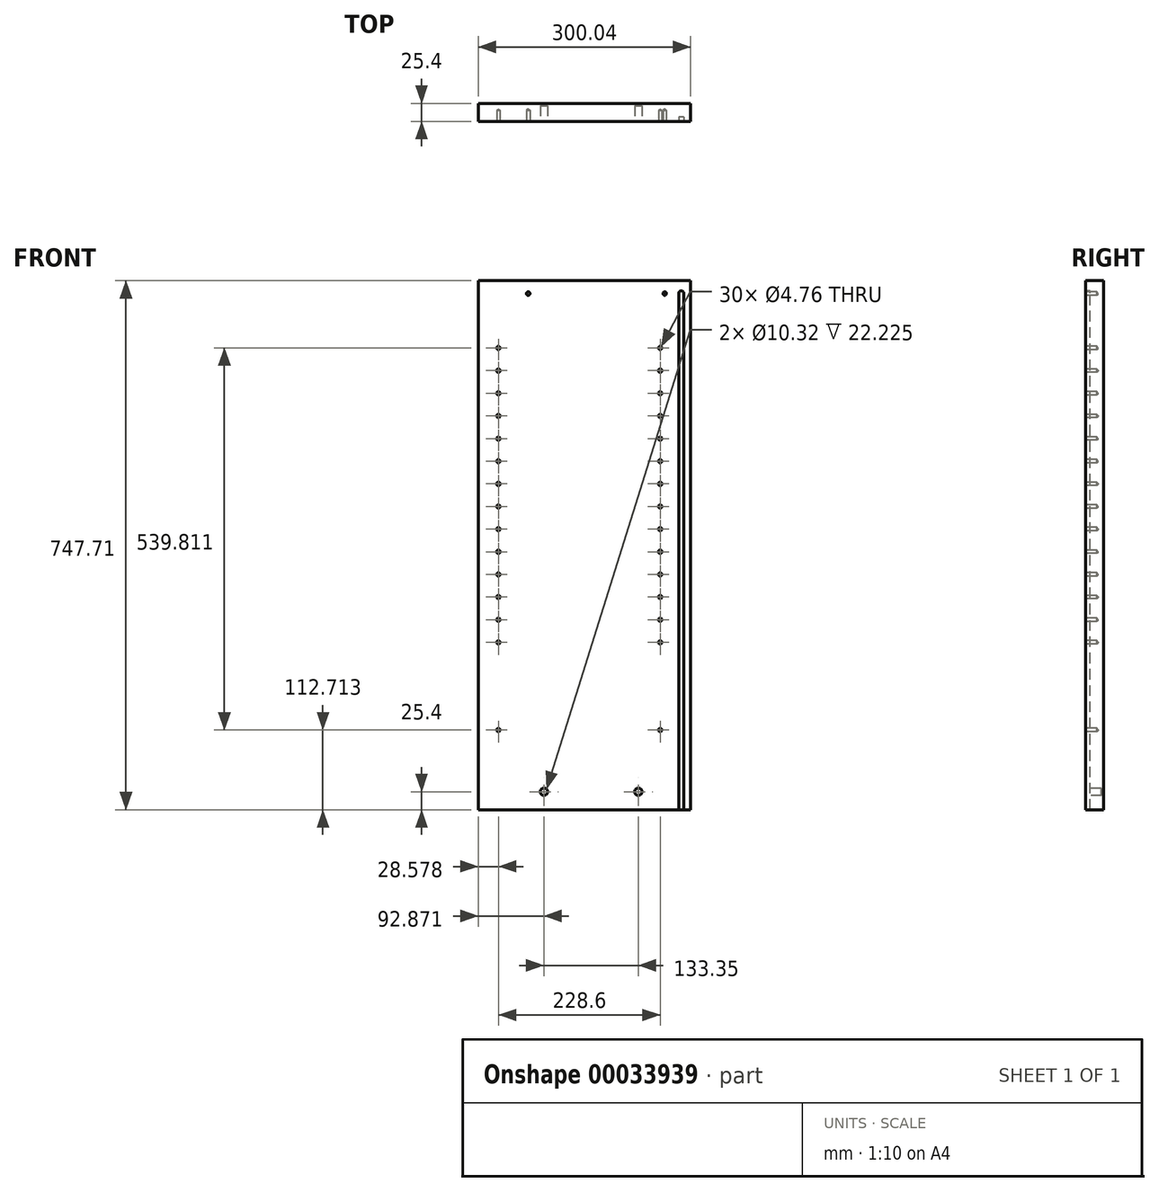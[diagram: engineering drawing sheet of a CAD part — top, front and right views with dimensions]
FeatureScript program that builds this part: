
annotation { "Feature Type Name" : "Feature", "Feature Type Description" : "" }
export const myFeature = defineFeature(function(context is Context, id is Id, definition is map)
    precondition{}
    {
        {
            var Q0;
            Q0=qCreatedBy(makeId("Front.planeOp"),FACE);
            var sketch = newSketch(context, id + "F0", { "sketchPlane" : qUnion([Q0])});
            skLineSegment(sketch, "E0.bottom", {"start": v(0, 0) * mm, "end": v(-300.04, 0) * mm});
            skLineSegment(sketch, "E0.top", {"start": v(0, 747.71) * mm, "end": v(-300.04, 747.71) * mm});
            skLineSegment(sketch, "E0.left", {"start": v(0, 0) * mm, "end": v(0, 747.71) * mm});
            skLineSegment(sketch, "E0.right", {"start": v(-300.04, 0) * mm, "end": v(-300.04, 747.71) * mm});
            skSolve(sketch);
        }
        {
            var Q0;
            Q0=makeQuery(id+"F0.imprint","IMPRINT",FACE,{"disambiguationData":[TD([[makeQuery(id+"F0.imprint","IMPRINT",EDGE,{"derivedFrom":sQuery(id+"F0.wireOp",EDGE,"E0.bottom")}),-1.0]])]});
            extrude(context, id + "F1", {"entities" : qUnion([Q0]), "depth" : 25.4 * mm});
        }
        {
            var Q0;
            Q0=makeQuery(id+"F1.opExtrude","CAP_FACE",FACE,{"disambiguationData":[OSD([sQuery(id+"F0.wireOp",EDGE,"E0.bottom"),sQuery(id+"F0.wireOp",EDGE,"E0.top"),sQuery(id+"F0.wireOp",EDGE,"E0.left"),sQuery(id+"F0.wireOp",EDGE,"E0.right")])],"isStart":false});
            var sketch = newSketch(context, id + "F2", { "sketchPlane" : qUnion([Q0])});
            skPoint(sketch, "E1", {"position": v(-271.46, 112.71) * mm});
            skPoint(sketch, "E2", {"position": v(-42.86, 112.71) * mm});
            skPoint(sketch, "E3", {"position": v(-42.86, 236.54) * mm});
            skPoint(sketch, "E4", {"position": v(-271.46, 236.54) * mm});
            skPoint(sketch, "E5.0.1.0", {"position": v(-271.46, 268.54) * mm});
            skPoint(sketch, "E5.0.1.1", {"position": v(-42.86, 268.54) * mm});
            skPoint(sketch, "E5.0.2.0", {"position": v(-271.46, 300.54) * mm});
            skPoint(sketch, "E5.0.2.1", {"position": v(-42.86, 300.54) * mm});
            skPoint(sketch, "E5.0.3.0", {"position": v(-271.46, 332.53) * mm});
            skPoint(sketch, "E5.0.3.1", {"position": v(-42.86, 332.53) * mm});
            skPoint(sketch, "E5.0.4.0", {"position": v(-271.46, 364.53) * mm});
            skPoint(sketch, "E5.0.4.1", {"position": v(-42.86, 364.53) * mm});
            skPoint(sketch, "E5.0.5.0", {"position": v(-271.46, 396.53) * mm});
            skPoint(sketch, "E5.0.5.1", {"position": v(-42.86, 396.53) * mm});
            skPoint(sketch, "E5.0.6.0", {"position": v(-271.46, 428.53) * mm});
            skPoint(sketch, "E5.0.6.1", {"position": v(-42.86, 428.53) * mm});
            skPoint(sketch, "E5.0.7.0", {"position": v(-271.46, 460.53) * mm});
            skPoint(sketch, "E5.0.7.1", {"position": v(-42.86, 460.53) * mm});
            skPoint(sketch, "E5.0.8.0", {"position": v(-271.46, 492.53) * mm});
            skPoint(sketch, "E5.0.8.1", {"position": v(-42.86, 492.53) * mm});
            skPoint(sketch, "E5.0.9.0", {"position": v(-271.46, 524.53) * mm});
            skPoint(sketch, "E5.0.9.1", {"position": v(-42.86, 524.53) * mm});
            skPoint(sketch, "E5.0.10.0", {"position": v(-271.46, 556.53) * mm});
            skPoint(sketch, "E5.0.10.1", {"position": v(-42.86, 556.53) * mm});
            skPoint(sketch, "E5.0.11.0", {"position": v(-271.46, 588.53) * mm});
            skPoint(sketch, "E5.0.11.1", {"position": v(-42.86, 588.53) * mm});
            skPoint(sketch, "E5.0.12.0", {"position": v(-271.46, 620.52) * mm});
            skPoint(sketch, "E5.0.12.1", {"position": v(-42.86, 620.52) * mm});
            skPoint(sketch, "E5.0.13.0", {"position": v(-271.46, 652.52) * mm});
            skPoint(sketch, "E5.0.13.1", {"position": v(-42.86, 652.52) * mm});
            skLineSegment(sketch, "E5.direction1", {"start": v(-271.46, 236.54) * mm, "end": v(-246.06, 236.54) * mm, "construction": true});
            skLineSegment(sketch, "E5.direction2", {"start": v(-271.46, 236.54) * mm, "end": v(-271.46, 268.54) * mm, "construction": true});
            skSolve(sketch);
        }
        {
            var Q0;
            Q0=sQuery(id+"F2.wireOp",VERTEX,"E1");
            var Q1;
            Q1=sQuery(id+"F2.wireOp",VERTEX,"E2");
            var Q2;
            Q2=sQuery(id+"F2.wireOp",VERTEX,"E4");
            var Q3;
            Q3=sQuery(id+"F2.wireOp",VERTEX,"E5.0.1.0");
            var Q4;
            Q4=sQuery(id+"F2.wireOp",VERTEX,"E3");
            var Q5;
            Q5=sQuery(id+"F2.wireOp",VERTEX,"E5.0.1.1");
            var Q6;
            Q6=sQuery(id+"F2.wireOp",VERTEX,"E5.0.2.1");
            var Q7;
            Q7=sQuery(id+"F2.wireOp",VERTEX,"E5.0.2.0");
            var Q8;
            Q8=sQuery(id+"F2.wireOp",VERTEX,"E5.0.3.0");
            var Q9;
            Q9=sQuery(id+"F2.wireOp",VERTEX,"E5.0.4.0");
            var Q10;
            Q10=sQuery(id+"F2.wireOp",VERTEX,"E5.0.5.0");
            var Q11;
            Q11=sQuery(id+"F2.wireOp",VERTEX,"E5.0.6.0");
            var Q12;
            Q12=sQuery(id+"F2.wireOp",VERTEX,"E5.0.7.0");
            var Q13;
            Q13=sQuery(id+"F2.wireOp",VERTEX,"E5.0.8.0");
            var Q14;
            Q14=sQuery(id+"F2.wireOp",VERTEX,"E5.0.9.0");
            var Q15;
            Q15=sQuery(id+"F2.wireOp",VERTEX,"E5.0.10.0");
            var Q16;
            Q16=sQuery(id+"F2.wireOp",VERTEX,"E5.0.12.0");
            var Q17;
            Q17=sQuery(id+"F2.wireOp",VERTEX,"E5.0.13.0");
            var Q18;
            Q18=sQuery(id+"F2.wireOp",VERTEX,"E5.0.3.1");
            var Q19;
            Q19=sQuery(id+"F2.wireOp",VERTEX,"E5.0.4.1");
            var Q20;
            Q20=sQuery(id+"F2.wireOp",VERTEX,"E5.0.5.1");
            var Q21;
            Q21=sQuery(id+"F2.wireOp",VERTEX,"E5.0.6.1");
            var Q22;
            Q22=sQuery(id+"F2.wireOp",VERTEX,"E5.0.4.1");
            var Q23;
            Q23=sQuery(id+"F2.wireOp",VERTEX,"E5.0.7.1");
            var Q24;
            Q24=sQuery(id+"F2.wireOp",VERTEX,"E5.0.8.1");
            var Q25;
            Q25=sQuery(id+"F2.wireOp",VERTEX,"E5.0.9.1");
            var Q26;
            Q26=sQuery(id+"F2.wireOp",VERTEX,"E5.0.10.1");
            var Q27;
            Q27=sQuery(id+"F2.wireOp",VERTEX,"E5.0.11.1");
            var Q28;
            Q28=sQuery(id+"F2.wireOp",VERTEX,"E5.0.12.1");
            var Q29;
            Q29=sQuery(id+"F2.wireOp",VERTEX,"E5.0.13.1");
            var Q30;
            Q30=sQuery(id+"F2.wireOp",VERTEX,"E5.0.11.0");
            var Q31;
            Q31=makeQuery(id+"F1.opExtrude","SWEPT_BODY",BODY,{"disambiguationData":[OSD([sQuery(id+"F0.wireOp",EDGE,"E0.bottom"),sQuery(id+"F0.wireOp",EDGE,"E0.top"),sQuery(id+"F0.wireOp",EDGE,"E0.left"),sQuery(id+"F0.wireOp",EDGE,"E0.right")])]});
            hole(context, id + "F3", {"style" : HoleStyle.SIMPLE, "holeDiameter" : 4.76 * mm, "endStyle" : HoleEndStyle.BLIND, "holeDepth" : 15.88 * mm, "locations" : qUnion([Q0, Q1, Q2, Q3, Q4, Q5, Q6, Q7, Q8, Q9, Q10, Q11, Q12, Q13, Q14, Q15, Q16, Q17, Q18, Q19, Q20, Q21, Q22, Q23, Q24, Q25, Q26, Q27, Q28, Q29, Q30]), "scope" : qUnion([Q31])});
        }
        {
            var Q0;
            Q0=makeQuery(id+"F1.opExtrude","CAP_FACE",FACE,{"disambiguationData":[OSD([sQuery(id+"F0.wireOp",EDGE,"E0.bottom"),sQuery(id+"F0.wireOp",EDGE,"E0.top"),sQuery(id+"F0.wireOp",EDGE,"E0.left"),sQuery(id+"F0.wireOp",EDGE,"E0.right")])],"isStart":false});
            var sketch = newSketch(context, id + "F4", { "sketchPlane" : qUnion([Q0])});
            skLineSegment(sketch, "E6.bottom", {"start": v(-9.53, 0) * mm, "end": v(-16.67, 0) * mm});
            skLineSegment(sketch, "E6.left", {"start": v(-9.53, 0) * mm, "end": v(-9.53, 729.85) * mm});
            skLineSegment(sketch, "E6.right", {"start": v(-16.67, 0) * mm, "end": v(-16.67, 729.85) * mm});
            skArc(sketch, "E7", {"start": v(-9.53, 729.85) * mm, "mid": v(-13.1, 733.42) * mm, "end": v(-16.67, 729.85) * mm});
            skSolve(sketch);
        }
        {
            var Q0;
            Q0 = qSketchRegion(id + "F4", true);
            extrude(context, id + "F5", {"entities" : qUnion([Q0]), "operationType" : NewBodyOperationType.REMOVE, "oppositeDirection" : true, "depth" : 6.35 * mm});
        }
        {
            var Q0;
            Q0=makeQuery(id+"F1.opExtrude","CAP_FACE",FACE,{"disambiguationData":[OSD([sQuery(id+"F0.wireOp",EDGE,"E0.bottom"),sQuery(id+"F0.wireOp",EDGE,"E0.top"),sQuery(id+"F0.wireOp",EDGE,"E0.left"),sQuery(id+"F0.wireOp",EDGE,"E0.right")])],"isStart":false});
            var sketch = newSketch(context, id + "F6", { "sketchPlane" : qUnion([Q0])});
            skCircle(sketch, "E8", {"center": v(-73.82, 25.4) * mm, "radius": 5.16 * mm});
            skCircle(sketch, "E9", {"center": v(-207.17, 25.4) * mm, "radius": 5.16 * mm});
            skSolve(sketch);
        }
        {
            var Q0;
            Q0 = qSketchRegion(id + "F6", true);
            extrude(context, id + "F7", {"entities" : qUnion([Q0]), "operationType" : NewBodyOperationType.REMOVE, "oppositeDirection" : true, "depth" : 22.22 * mm});
        }
        {
            var Q0;
            Q0=makeQuery(id+"F1.opExtrude","CAP_FACE",FACE,{"disambiguationData":[OSD([sQuery(id+"F0.wireOp",EDGE,"E0.bottom"),sQuery(id+"F0.wireOp",EDGE,"E0.top"),sQuery(id+"F0.wireOp",EDGE,"E0.left"),sQuery(id+"F0.wireOp",EDGE,"E0.right")])],"isStart":false});
            var sketch = newSketch(context, id + "F8", { "sketchPlane" : qUnion([Q0])});
            skPoint(sketch, "E10", {"position": v(-229.4, 729.46) * mm});
            skPoint(sketch, "E11", {"position": v(-36.51, 729.46) * mm});
            skSolve(sketch);
        }
        {
            var Q0;
            Q0=sQuery(id+"F8.wireOp",VERTEX,"E10");
            var Q1;
            Q1=sQuery(id+"F8.wireOp",VERTEX,"E11");
            var Q2;
            Q2=makeQuery(id+"F1.opExtrude","SWEPT_BODY",BODY,{"disambiguationData":[OSD([sQuery(id+"F0.wireOp",EDGE,"E0.bottom"),sQuery(id+"F0.wireOp",EDGE,"E0.top"),sQuery(id+"F0.wireOp",EDGE,"E0.left"),sQuery(id+"F0.wireOp",EDGE,"E0.right")])]});
            hole(context, id + "F9", {"style" : HoleStyle.SIMPLE, "holeDiameter" : 5 * mm, "endStyle" : HoleEndStyle.BLIND, "holeDepth" : 15.88 * mm, "locations" : qUnion([Q0, Q1]), "scope" : qUnion([Q2])});
        }
    });
